# Revit family: WashbasinUnit-BoxFor80cmUnit-Vitra-İntegraSeries-65608+65588+65587
name_source: partatom
category: Furniture Systems
revit_build: Autodesk Revit 2017 (Build: 20160225_1515(x64)
units: mm (PartAtom-declared; Revit-internal decimal feet)

## family parameters
Cut with Voids When Loaded = No
Host = Face
OmniClass Number = 23.40.00.00
OmniClass Title = Equipment and Furnishings
Part Type = Normal
Room Calculation Point = No
Round Connector Dimension = Use Diameter
Shared = Yes

## types (3) — shared parameters
BIMobject category = Bathroom compound units
Brand = VitrA
Construction Type = Floor Mounted
Depth(mm) = 388 mm
Description = Box for 80cm unit
Design country = Turkey
Height(mm) = 264 mm
IFC Classification = Furniture
Manufacturer = Vitra
Manufacturer name = Vitra
Masterformat 2014 Code = 13 42 13
Masterformat 2014 Description = Bathroom Unit Modules
NBS Referans Code = 35-75-08
NBS Referans Description = Bathroom Cabinets
Nominal height = 0.000
Nominal width = 0.000
OmniClass Code = 23-31 25 13
OmniClass Description = Bathroom Cabinets
Product certification = https://vitraglobal.com
Product data url = https://www.vitra-bad.fr
Product family = İntegra
Product group = Washbasin Unit box
Technical description = http://cdn.vitra.com.tr
UNSPSC Code = 301815
UNSPSC Description = Bathroom Cabinets
URL = https://vitraglobal.com
Uniclass 1.4 Code = L8241
Uniclass 1.4 Description = Bathroom Cabinets
Uniclass 2.0 Code = PR-35-75-08
Uniclass 2.0 Description = Bathroom Cabinets
Uniclass 2015 Code = Pr_40_20_93
Uniclass 2015 Name = Wash basins, sinks and troughs
Uniformat II Code = E20
Uniformat II Description = FURNISHINGS
Warranty Period (Year) = 2
Weight Net (kg) = 6,3
Width(mm) = 764 mm  [stored 2.50656 ft]
Youtube = https://www.youtube.com
zero-valued in all types: Default Elevation

## per-type parameters (varying)
| type | Article No. (default) | Color | Model | Primary Material | Product SKU |
| WashbasinUnit-BoxFor80cmUnit-Vitra-İntegraSeries-65587 | 65587 | White | 65587 | White | 65587 |
| WashbasinUnit-BoxFor80cmUnit-Vitra-İntegraSeries-65588 | 65588 | Anthracite Gray | 65588 | Anthracite Gray | 65588 |
| WashbasinUnit-BoxFor80cmUnit-Vitra-İntegraSeries-65608 | 65608 | natural gray oak | 65608 | natural gray oak | 65608 |

note: [stored X ft] marks values corroborated as IEEE doubles in the binary element streams (Revit-internal decimal feet)

## geometry (parser evidence)
native form markers: Sweep x2
no freeform markers — native parametric forms only
